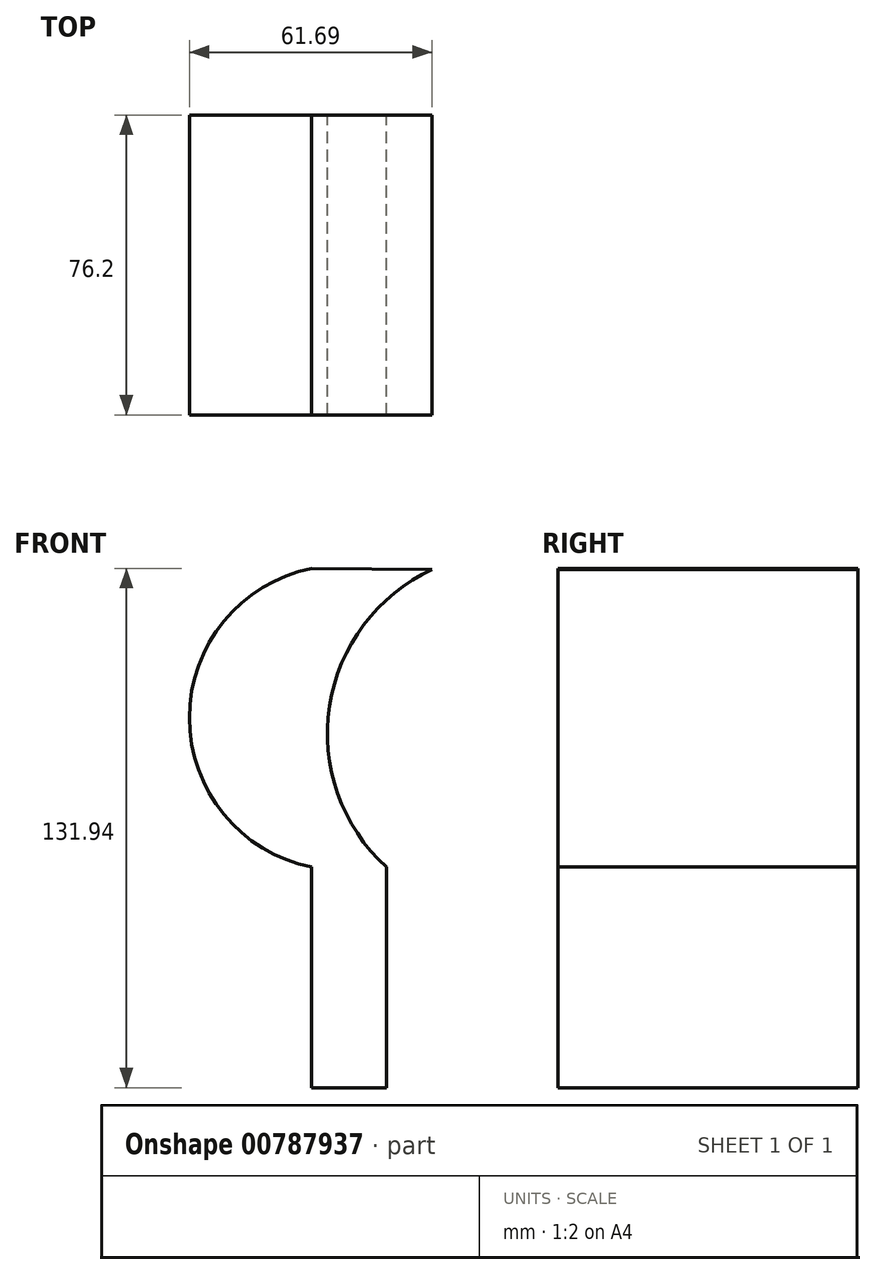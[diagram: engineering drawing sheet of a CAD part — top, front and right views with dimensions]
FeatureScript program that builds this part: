
annotation { "Feature Type Name" : "Feature", "Feature Type Description" : "" }
export const myFeature = defineFeature(function(context is Context, id is Id, definition is map)
    precondition{}
    {
        {
            var Q0;
            Q0=qCreatedBy(makeId("Front.planeOp"),FACE);
            var sketch = newSketch(context, id + "F0", { "sketchPlane" : qUnion([Q0])});
            skLineSegment(sketch, "E0", {"start": v(-29.08, 0) * mm, "end": v(-29.08, -56.04) * mm});
            skLineSegment(sketch, "E1", {"start": v(-29.08, -56.04) * mm, "end": v(-48.1, -56.04) * mm});
            skLineSegment(sketch, "E2", {"start": v(-48.1, -56.04) * mm, "end": v(-48.1, 0) * mm});
            skArc(sketch, "E3", {"start": v(-48.1, 75.9) * mm, "mid": v(-79.14, 37.95) * mm, "end": v(-48.1, 0) * mm});
            skArc(sketch, "E4", {"start": v(-17.45, 75.61) * mm, "mid": v(-43.52, 40.92) * mm, "end": v(-29.08, 0) * mm});
            skLineSegment(sketch, "E5", {"start": v(-48.1, 75.9) * mm, "end": v(-17.45, 75.61) * mm});
            skSolve(sketch);
        }
        {
            var Q0;
            Q0 = qSketchRegion(id + "F0", true);
            extrude(context, id + "F1", {"entities" : qUnion([Q0]), "depth" : 76.2 * mm, "offsetDistance" : 25.4 * mm});
        }
    });
